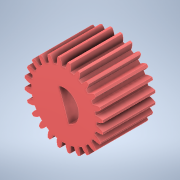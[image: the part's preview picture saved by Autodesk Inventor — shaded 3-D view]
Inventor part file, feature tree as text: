
AUTODESK INVENTOR PART (.ipt)
format: ipt  version: 2022 (Build 260153000, 153)  size: 253,952 bytes
history: mixed  units: in
note: dims shown in document units (in); Inventor stores cm internally (conversion verified against a paired STEP export)
features: direct_edit x1, extrude x1, sketch x1, other x1, move_body x1, imported_body x1
ambient origin geometry x8: Origin, YZ Plane, XZ Plane, XY Plane, X Axis, Y Axis, Z Axis, Center Point
bodies: Solid1 (imported_parasolid)
feature tree (6):
  direct_edit  "Direct Edit1"
  extrude  "Extrusion3"  Depth=0.1703in TaperAngle=0.0deg
  sketch  "Sketch3"  dims[d0=0.0in d1=0.0in d2=-0.25in d9=0.1703in d10=0.0in]
  other  "24_Teeth_Sun_Gear.STEP"
  move_body  "Move1"
  imported_body  NMx_Import_Brep_tag  [imported B-rep: ~101 faces, bbox_mm=[8.65, 12.93135, 12.93135]]
